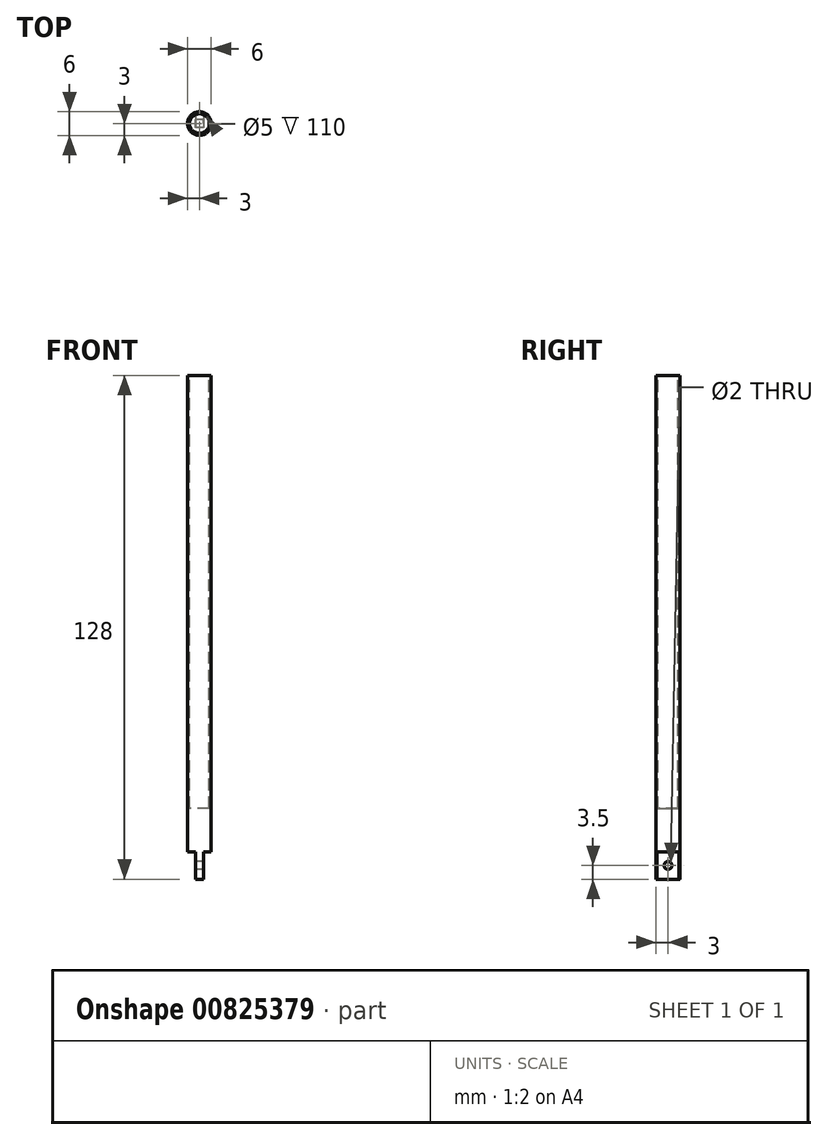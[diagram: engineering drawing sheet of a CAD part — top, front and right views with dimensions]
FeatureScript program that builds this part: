
annotation { "Feature Type Name" : "Feature", "Feature Type Description" : "" }
export const myFeature = defineFeature(function(context is Context, id is Id, definition is map)
    precondition{}
    {
        {
            var Q0;
            Q0=qCreatedBy(makeId("Top.planeOp"),FACE);
            var sketch = newSketch(context, id + "F0", { "sketchPlane" : qUnion([Q0])});
            skCircle(sketch, "E0", {"center": v(0, 0) * mm, "radius": 3 * mm});
            skSolve(sketch);
        }
        {
            var Q0;
            Q0 = qSketchRegion(id + "F0", true);
            extrude(context, id + "F1", {"entities" : qUnion([Q0]), "depth" : 128 * mm, "offsetDistance" : 25 * mm});
        }
        {
            var Q0;
            Q0=makeQuery(id+"F1.opExtrude","CAP_FACE",FACE,{"disambiguationData":[OSD([sQuery(id+"F0.wireOp",EDGE,"E0")])],"isStart":false});
            var sketch = newSketch(context, id + "F2", { "sketchPlane" : qUnion([Q0])});
            skCircle(sketch, "E1", {"center": v(0, 0) * mm, "radius": 2.5 * mm});
            skSolve(sketch);
        }
        {
            var Q0;
            Q0 = qSketchRegion(id + "F2", true);
            extrude(context, id + "F3", {"entities" : qUnion([Q0]), "operationType" : NewBodyOperationType.REMOVE, "oppositeDirection" : true, "depth" : 110 * mm, "offsetDistance" : 25 * mm});
        }
        {
            var Q0;
            Q0=qCreatedBy(makeId("Front.planeOp"),FACE);
            var sketch = newSketch(context, id + "F4", { "sketchPlane" : qUnion([Q0])});
            skLineSegment(sketch, "E2", {"start": v(0, 0) * mm, "end": v(1, 0) * mm, "construction": true});
            skLineSegment(sketch, "E3", {"start": v(0, 0) * mm, "end": v(-1, 0) * mm, "construction": true});
            skLineSegment(sketch, "E4", {"start": v(0, 0) * mm, "end": v(0, 7) * mm, "construction": true});
            skLineSegment(sketch, "E5.bottom", {"start": v(1, 0) * mm, "end": v(3.84, 0) * mm});
            skLineSegment(sketch, "E5.top", {"start": v(1, 7) * mm, "end": v(3.84, 7) * mm});
            skLineSegment(sketch, "E5.left", {"start": v(1, 0) * mm, "end": v(1, 7) * mm});
            skLineSegment(sketch, "E5.right", {"start": v(3.84, 0) * mm, "end": v(3.84, 7) * mm});
            skLineSegment(sketch, "E6.MirrorCS", {"start": v(-3.84, 0) * mm, "end": v(-3.84, 7) * mm});
            skLineSegment(sketch, "E7.MirrorCS", {"start": v(-1, 7) * mm, "end": v(-3.84, 7) * mm});
            skLineSegment(sketch, "E8.MirrorCS", {"start": v(-1, 0) * mm, "end": v(-1, 7) * mm});
            skLineSegment(sketch, "E9.MirrorCS", {"start": v(-1, 0) * mm, "end": v(-3.84, 0) * mm});
            skSolve(sketch);
        }
        {
            var Q0;
            Q0 = qSketchRegion(id + "F4", true);
            extrude(context, id + "F5", {"entities" : qUnion([Q0]), "operationType" : NewBodyOperationType.REMOVE, "endBound" : BoundingType.SYMMETRIC, "oppositeDirection" : true, "depth" : 25 * mm, "offsetDistance" : 25 * mm});
        }
        {
            var Q0;
            Q0=makeQuery(id+"F5.boolean.opBoolean","COPY",FACE,{"derivedFrom":makeQuery(id+"F5.opExtrude","SWEPT_FACE",FACE,{"disambiguationData":[OSD([sQuery(id+"F4.wireOp",EDGE,"E8.MirrorCS")])]})});
            var sketch = newSketch(context, id + "F6", { "sketchPlane" : qUnion([Q0])});
            skCircle(sketch, "E10", {"center": v(0, 3.5) * mm, "radius": 1 * mm});
            skPoint(sketch, "E10.centerSnap0", {"position": v(-2.83, 3.5) * mm});
            skPoint(sketch, "E10.centerSnap1", {"position": v(0, 7) * mm});
            skSolve(sketch);
        }
        {
            var Q0;
            Q0 = qSketchRegion(id + "F6", true);
            extrude(context, id + "F7", {"entities" : qUnion([Q0]), "operationType" : NewBodyOperationType.REMOVE, "endBound" : BoundingType.THROUGH_ALL, "oppositeDirection" : true, "depth" : 25 * mm, "offsetDistance" : 25 * mm});
        }
    });
